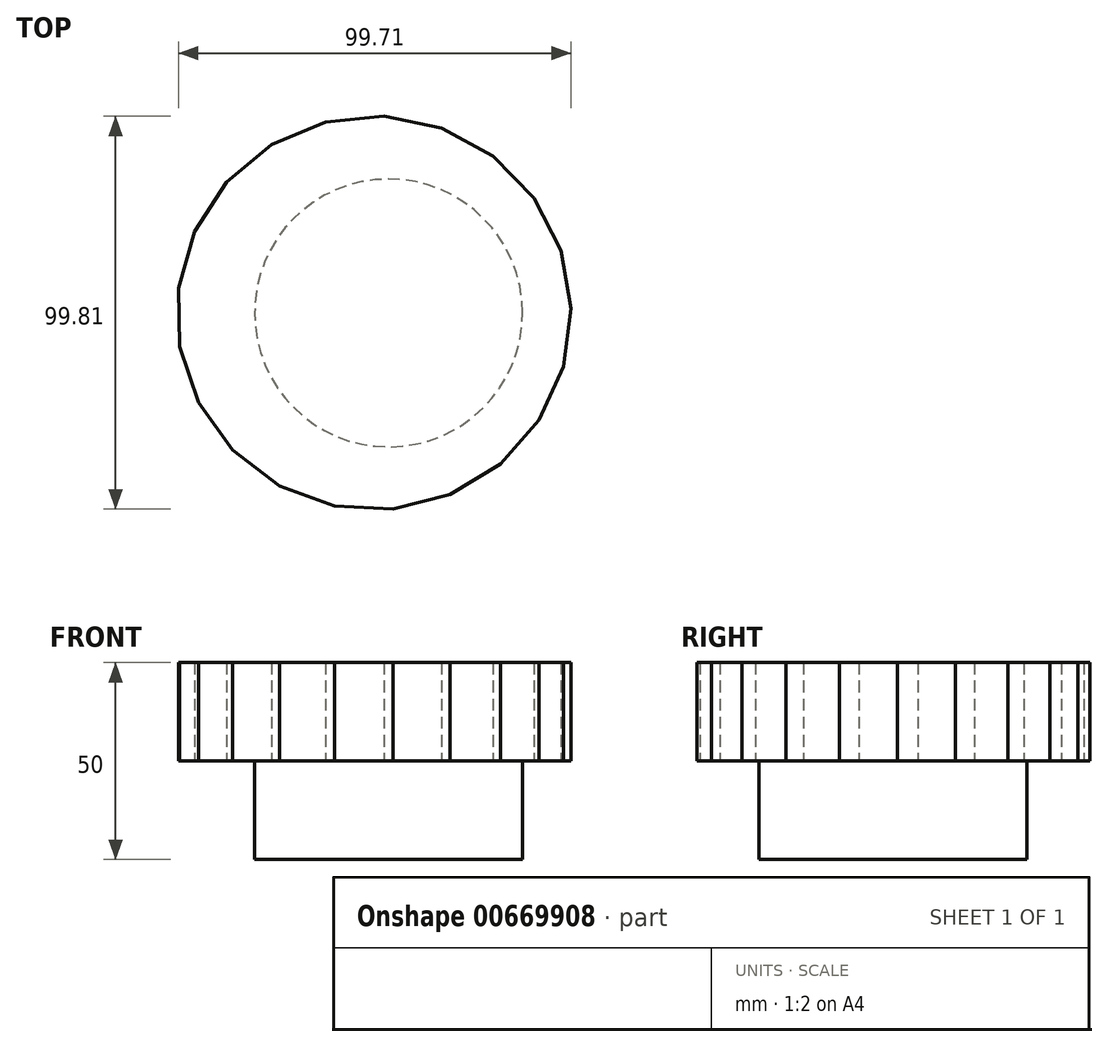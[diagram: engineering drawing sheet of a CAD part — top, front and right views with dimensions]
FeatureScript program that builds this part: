
annotation { "Feature Type Name" : "Feature", "Feature Type Description" : "" }
export const myFeature = defineFeature(function(context is Context, id is Id, definition is map)
    precondition{}
    {
        {
            var Q0;
            Q0=qCreatedBy(makeId("Top.planeOp"),FACE);
            var sketch = newSketch(context, id + "F0", { "sketchPlane" : qUnion([Q0])});
            skCircle(sketch, "E0", {"center": v(3.73, 0) * mm, "radius": 34.03 * mm});
            skSolve(sketch);
        }
        {
            var Q0;
            Q0=makeQuery(id+"F0.imprint","IMPRINT",FACE,{"disambiguationData":[TD([[makeQuery(id+"F0.imprint","IMPRINT",EDGE,{"derivedFrom":sQuery(id+"F0.wireOp",EDGE,"E0")}),1.0]])]});
            extrude(context, id + "F1", {"entities" : qUnion([Q0]), "depth" : 25 * mm, "offsetDistance" : 25 * mm});
        }
        {
            var Q0;
            Q0=makeQuery(id+"F1.opExtrude","CAP_FACE",FACE,{"disambiguationData":[OSD([sQuery(id+"F0.wireOp",EDGE,"E0")])],"isStart":false});
            var sketch = newSketch(context, id + "F2", { "sketchPlane" : qUnion([Q0])});
            skCircle(sketch, "E1.cCircle", {"center": v(0, 0) * mm, "radius": 49.5 * mm, "construction": true});
            skLineSegment(sketch, "E1.0", {"start": v(-12.25, 48.54) * mm, "end": v(2.6, 50) * mm});
            skLineSegment(sketch, "E1.1", {"start": v(2.6, 50) * mm, "end": v(17.22, 47) * mm});
            skLineSegment(sketch, "E1.2", {"start": v(17.22, 47) * mm, "end": v(30.3, 39.84) * mm});
            skLineSegment(sketch, "E1.3", {"start": v(30.3, 39.84) * mm, "end": v(40.7, 29.14) * mm});
            skLineSegment(sketch, "E1.4", {"start": v(40.7, 29.14) * mm, "end": v(47.49, 15.85) * mm});
            skLineSegment(sketch, "E1.5", {"start": v(47.49, 15.85) * mm, "end": v(50.05, 1.15) * mm});
            skLineSegment(sketch, "E1.6", {"start": v(50.05, 1.15) * mm, "end": v(48.16, -13.66) * mm});
            skLineSegment(sketch, "E1.7", {"start": v(48.16, -13.66) * mm, "end": v(42, -27.25) * mm});
            skLineSegment(sketch, "E1.8", {"start": v(42, -27.25) * mm, "end": v(32.1, -38.41) * mm});
            skLineSegment(sketch, "E1.9", {"start": v(32.1, -38.41) * mm, "end": v(19.35, -46.17) * mm});
            skLineSegment(sketch, "E1.10", {"start": v(19.35, -46.17) * mm, "end": v(4.88, -49.82) * mm});
            skLineSegment(sketch, "E1.11", {"start": v(4.88, -49.82) * mm, "end": v(-10.02, -49.05) * mm});
            skLineSegment(sketch, "E1.12", {"start": v(-10.02, -49.05) * mm, "end": v(-24.03, -43.91) * mm});
            skLineSegment(sketch, "E1.13", {"start": v(-24.03, -43.91) * mm, "end": v(-35.9, -34.88) * mm});
            skLineSegment(sketch, "E1.14", {"start": v(-35.9, -34.88) * mm, "end": v(-44.6, -22.75) * mm});
            skLineSegment(sketch, "E1.15", {"start": v(-44.6, -22.75) * mm, "end": v(-49.32, -8.6) * mm});
            skLineSegment(sketch, "E1.16", {"start": v(-49.32, -8.6) * mm, "end": v(-49.66, 6.33) * mm});
            skLineSegment(sketch, "E1.17", {"start": v(-49.66, 6.33) * mm, "end": v(-45.59, 20.68) * mm});
            skLineSegment(sketch, "E1.18", {"start": v(-45.59, 20.68) * mm, "end": v(-37.47, 33.2) * mm});
            skLineSegment(sketch, "E1.19", {"start": v(-37.47, 33.2) * mm, "end": v(-26.02, 42.77) * mm});
            skLineSegment(sketch, "E1.20", {"start": v(-26.02, 42.77) * mm, "end": v(-12.25, 48.54) * mm});
            skPoint(sketch, "E1.0.midPoint", {"position": v(-4.83, 49.27) * mm});
            skSolve(sketch);
        }
        {
            var Q0;
            Q0 = qSketchRegion(id + "F2", true);
            extrude(context, id + "F3", {"entities" : qUnion([Q0]), "operationType" : NewBodyOperationType.ADD, "depth" : 25 * mm, "offsetDistance" : 25 * mm});
        }
    });
